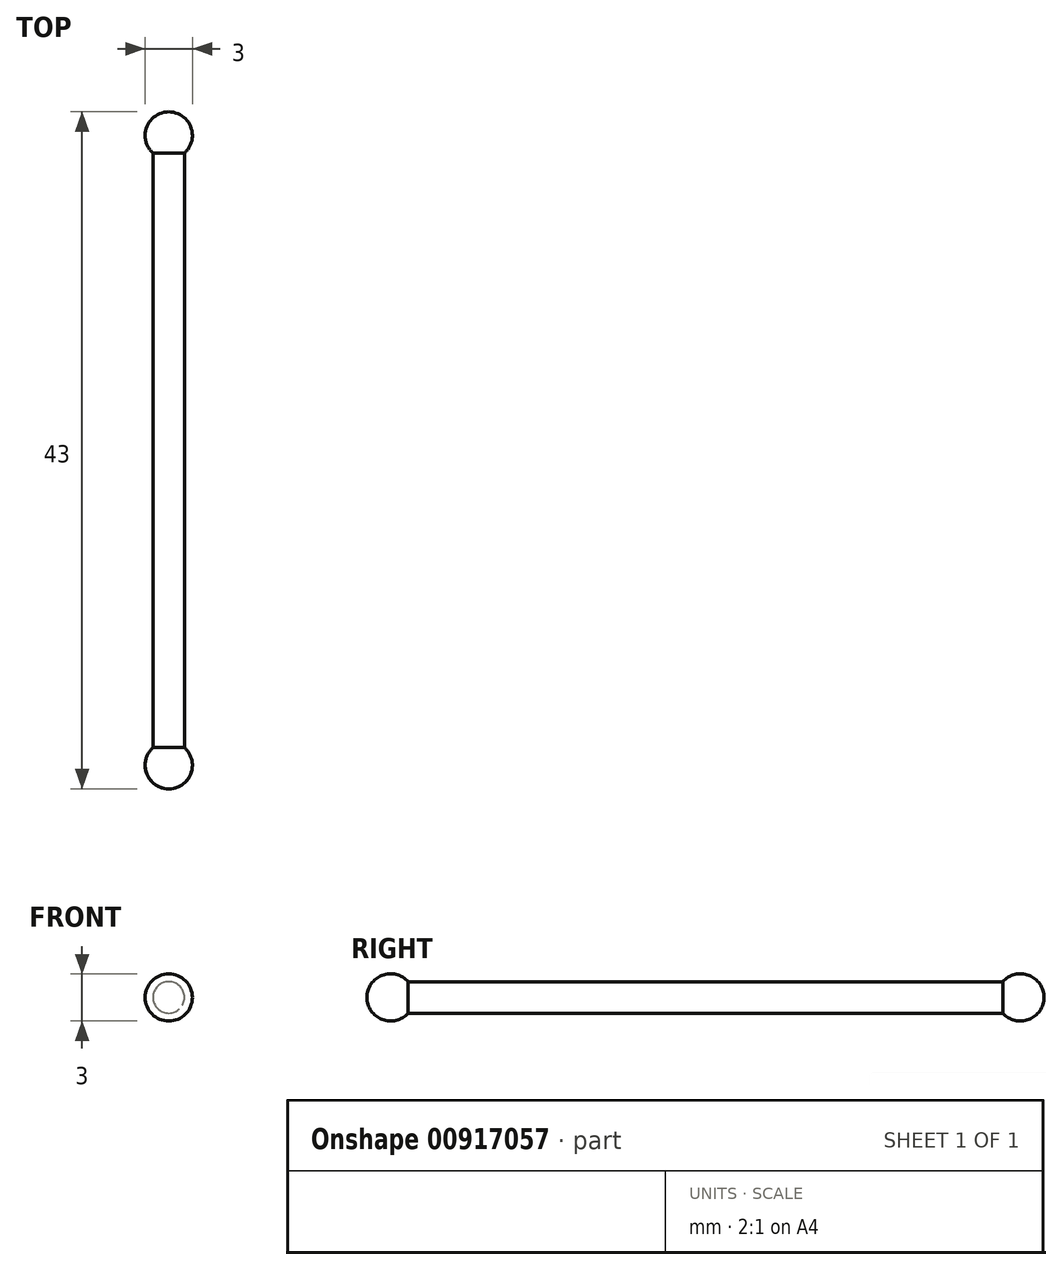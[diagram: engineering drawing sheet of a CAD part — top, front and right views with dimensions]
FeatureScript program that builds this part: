
annotation { "Feature Type Name" : "Feature", "Feature Type Description" : "" }
export const myFeature = defineFeature(function(context is Context, id is Id, definition is map)
    precondition{}
    {
        {
            var Q0;
            Q0=qCreatedBy(makeId("Front.planeOp"),FACE);
            var sketch = newSketch(context, id + "F0", { "sketchPlane" : qUnion([Q0])});
            skCircle(sketch, "E0", {"center": v(0, 0) * mm, "radius": 1 * mm});
            skSolve(sketch);
        }
        {
            var Q0;
            Q0=makeQuery(id+"F0.imprint","IMPRINT",FACE,{"disambiguationData":[TD([[makeQuery(id+"F0.imprint","IMPRINT",EDGE,{"derivedFrom":sQuery(id+"F0.wireOp",EDGE,"E0")}),1.0]])]});
            extrude(context, id + "F1", {"entities" : qUnion([Q0]), "endBound" : BoundingType.SYMMETRIC, "depth" : 40 * mm, "offsetDistance" : 25 * mm});
        }
        {
            var Q0;
            Q0=qCreatedBy(makeId("Top.planeOp"),FACE);
            var sketch = newSketch(context, id + "F2", { "sketchPlane" : qUnion([Q0])});
            skArc(sketch, "E1", {"start": v(-1.5, -20) * mm, "mid": v(0, -21.5) * mm, "end": v(1.5, -20) * mm});
            skPoint(sketch, "E2.orphan", {"position": v(-1, -20) * mm});
            skPoint(sketch, "E3.0.start.orphan", {"position": v(1, -20) * mm});
            skLineSegment(sketch, "E4", {"start": v(-1.5, -20) * mm, "end": v(1.5, -20) * mm});
            skSolve(sketch);
        }
        {
            var Q0;
            Q0=makeQuery(id+"F2.imprint","IMPRINT",FACE,{"disambiguationData":[TD([[makeQuery(id+"F2.imprint","IMPRINT",EDGE,{"derivedFrom":sQuery(id+"F2.wireOp",EDGE,"E1")}),1.0]])]});
            var Q1;
            Q1=sQuery(id+"F2.wireOp",EDGE,"E4");
            revolve(context, id + "F3", {"operationType" : NewBodyOperationType.ADD, "surfaceOperationType" : NewSurfaceOperationType.NEW, "entities" : qUnion([Q0]), "axis" : qUnion([Q1]), "revolveType" : RevolveType.FULL});
        }
        {
            var Q0;
            Q0=qCreatedBy(makeId("Top.planeOp"),FACE);
            var sketch = newSketch(context, id + "F4", { "sketchPlane" : qUnion([Q0])});
            skArc(sketch, "E5", {"start": v(1.5, 20) * mm, "mid": v(0, 21.5) * mm, "end": v(-1.5, 20) * mm});
            skPoint(sketch, "E6.orphan", {"position": v(-1, 20) * mm});
            skPoint(sketch, "E7.0.start.orphan", {"position": v(1, 20) * mm});
            skLineSegment(sketch, "E8", {"start": v(-1.5, 20) * mm, "end": v(1.5, 20) * mm});
            skSolve(sketch);
        }
        {
            var Q0;
            Q0=makeQuery(id+"F4.imprint","IMPRINT",FACE,{"disambiguationData":[TD([[makeQuery(id+"F4.imprint","IMPRINT",EDGE,{"derivedFrom":sQuery(id+"F4.wireOp",EDGE,"E5")}),1.0]])]});
            var Q1;
            Q1=sQuery(id+"F4.wireOp",EDGE,"E8");
            revolve(context, id + "F5", {"operationType" : NewBodyOperationType.ADD, "surfaceOperationType" : NewSurfaceOperationType.NEW, "entities" : qUnion([Q0]), "axis" : qUnion([Q1]), "revolveType" : RevolveType.FULL});
        }
    });
